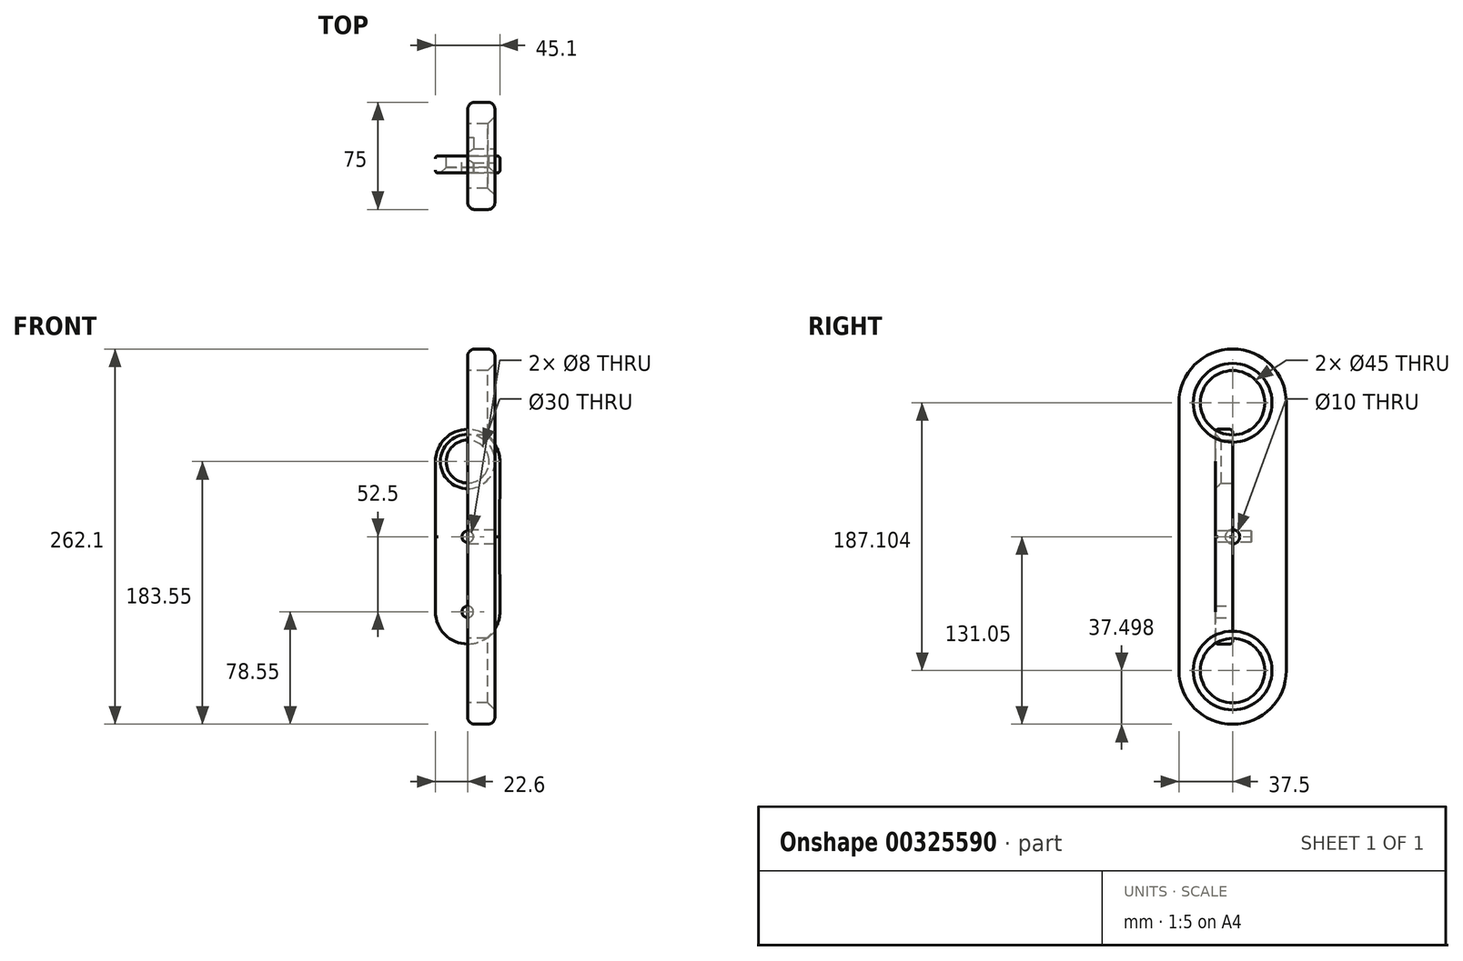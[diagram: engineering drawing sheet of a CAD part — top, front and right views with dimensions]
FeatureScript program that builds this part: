
annotation { "Feature Type Name" : "Feature", "Feature Type Description" : "" }
export const myFeature = defineFeature(function(context is Context, id is Id, definition is map)
    precondition{}
    {
        {
            var Q0;
            Q0=qCreatedBy(makeId("Right.planeOp"),FACE);
            var sketch = newSketch(context, id + "F0", { "sketchPlane" : qUnion([Q0])});
            skCircle(sketch, "E0", {"center": v(0, 93.55) * mm, "radius": 22.5 * mm});
            skArc(sketch, "E1", {"start": v(37.5, 93.55) * mm, "mid": v(0, 131.05) * mm, "end": v(-37.5, 93.55) * mm});
            skLineSegment(sketch, "E2", {"start": v(-37.5, 93.55) * mm, "end": v(-37.5, 0) * mm});
            skLineSegment(sketch, "E3", {"start": v(37.5, 0) * mm, "end": v(37.5, 93.55) * mm});
            skCircle(sketch, "E4.MirrorC", {"center": v(0, -93.55) * mm, "radius": 22.5 * mm});
            skArc(sketch, "E5.MirrorCS", {"start": v(37.5, -93.55) * mm, "mid": v(0, -131.05) * mm, "end": v(-37.5, -93.55) * mm});
            skLineSegment(sketch, "E6.MirrorCS", {"start": v(-37.5, -93.55) * mm, "end": v(-37.5, 0) * mm});
            skLineSegment(sketch, "E7.MirrorCS", {"start": v(37.5, 0) * mm, "end": v(37.5, -93.55) * mm});
            skSolve(sketch);
        }
        {
            var Q0;
            Q0 = qSketchRegion(id + "F0", true);
            extrude(context, id + "F1", {"entities" : qUnion([Q0]), "depth" : 19 * mm});
        }
        {
            var Q0;
            Q0=makeQuery(id+"F1.opExtrude","CAP_EDGE",EDGE,{"disambiguationData":[OSD([sQuery(id+"F0.wireOp",EDGE,"E0")])],"isStart":false});
            var Q1;
            Q1=makeQuery(id+"F1.opExtrude","CAP_EDGE",EDGE,{"disambiguationData":[OSD([sQuery(id+"F0.wireOp",EDGE,"E4.MirrorC")])],"isStart":false});
            chamfer(context, id + "F2", {"entities" : qUnion([Q0, Q1]), "width" : 5 * mm, "tangentPropagation" : true});
        }
        {
            var Q0;
            Q0=qCreatedBy(makeId("Right.planeOp"),FACE);
            var sketch = newSketch(context, id + "F3", { "sketchPlane" : qUnion([Q0])});
            skCircle(sketch, "E8", {"center": v(0, 0) * mm, "radius": 5 * mm});
            skSolve(sketch);
        }
        {
            var Q0;
            Q0 = qSketchRegion(id + "F3", true);
            extrude(context, id + "F4", {"entities" : qUnion([Q0]), "operationType" : NewBodyOperationType.REMOVE, "endBound" : BoundingType.SYMMETRIC, "oppositeDirection" : true, "depth" : 40 * mm});
        }
        {
            var Q0;
            Q0=makeQuery(id+"F1.opExtrude","CAP_EDGE",EDGE,{"disambiguationData":[OSD([sQuery(id+"F0.wireOp",EDGE,"E2"),sQuery(id+"F0.wireOp",EDGE,"E6.MirrorCS")])],"isStart":false});
            var Q1;
            Q1=makeQuery(id+"F1.opExtrude","CAP_EDGE",EDGE,{"disambiguationData":[OSD([sQuery(id+"F0.wireOp",EDGE,"E1")])],"isStart":true});
            fillet(context, id + "F5", {"entities" : qUnion([Q0, Q1]), "radius" : 5 * mm, "tangentPropagation" : true, "allowEdgeOverflow" : false});
        }
        {
            var Q0;
            Q0=qCreatedBy(makeId("Front.planeOp"),FACE);
            var sketch = newSketch(context, id + "F6", { "sketchPlane" : qUnion([Q0])});
            skCircle(sketch, "E9", {"center": v(0, 52.5) * mm, "radius": 15 * mm});
            skArc(sketch, "E10", {"start": v(22.5, 52.46) * mm, "mid": v(0.04, 75) * mm, "end": v(-22.5, 52.54) * mm});
            skLineSegment(sketch, "E11", {"start": v(-22.6, 0) * mm, "end": v(-22.5, 52.54) * mm});
            skLineSegment(sketch, "E12", {"start": v(22.4, 0) * mm, "end": v(22.5, 52.46) * mm});
            skLineSegment(sketch, "E13.MirrorCS", {"start": v(22.4, 0) * mm, "end": v(22.5, -52.46) * mm});
            skArc(sketch, "E14.MirrorC", {"start": v(22.5, -52.46) * mm, "mid": v(0.04, -75) * mm, "end": v(-22.5, -52.54) * mm});
            skLineSegment(sketch, "E15.MirrorCS", {"start": v(-22.6, 0) * mm, "end": v(-22.5, -52.54) * mm});
            skCircle(sketch, "E16", {"center": v(0, -52.5) * mm, "radius": 4 * mm});
            skSolve(sketch);
        }
        {
            var Q0;
            Q0 = qSketchRegion(id + "F6", true);
            extrude(context, id + "F7", {"entities" : qUnion([Q0]), "depth" : 12 * mm});
        }
        {
            var Q0;
            Q0=makeQuery(id+"F7.opExtrude","CAP_EDGE",EDGE,{"disambiguationData":[OSD([sQuery(id+"F6.wireOp",EDGE,"E9")])],"isStart":false});
            chamfer(context, id + "F8", {"entities" : qUnion([Q0]), "width" : 4 * mm, "tangentPropagation" : true});
        }
        {
            var Q0;
            Q0=makeQuery(id+"F7.opExtrude","CAP_EDGE",EDGE,{"disambiguationData":[OSD([sQuery(id+"F6.wireOp",EDGE,"E11")])],"isStart":false});
            var Q1;
            Q1=makeQuery(id+"F7.opExtrude","CAP_EDGE",EDGE,{"disambiguationData":[OSD([sQuery(id+"F6.wireOp",EDGE,"E12")])],"isStart":true});
            var Q2;
            Q2=makeQuery(id+"F7.opExtrude","CAP_EDGE",EDGE,{"disambiguationData":[OSD([sQuery(id+"F6.wireOp",EDGE,"E14.MirrorC")])],"isStart":false});
            var Q3;
            Q3=makeQuery(id+"F7.opExtrude","CAP_EDGE",EDGE,{"disambiguationData":[OSD([sQuery(id+"F6.wireOp",EDGE,"E14.MirrorC")])],"isStart":true});
            fillet(context, id + "F9", {"entities" : qUnion([Q0, Q1, Q2, Q3]), "radius" : 2 * mm, "tangentPropagation" : true, "allowEdgeOverflow" : false});
        }
        {
            var Q0;
            Q0=makeQuery(id+"F7.opExtrude","CAP_FACE",FACE,{"disambiguationData":[OSD([sQuery(id+"F6.wireOp",EDGE,"E9"),sQuery(id+"F6.wireOp",EDGE,"E10"),sQuery(id+"F6.wireOp",EDGE,"E11"),sQuery(id+"F6.wireOp",EDGE,"E12"),sQuery(id+"F6.wireOp",EDGE,"E13.MirrorCS"),sQuery(id+"F6.wireOp",EDGE,"E14.MirrorC"),sQuery(id+"F6.wireOp",EDGE,"E15.MirrorCS"),sQuery(id+"F6.wireOp",EDGE,"E16")])],"isStart":false});
            var sketch = newSketch(context, id + "F10", { "sketchPlane" : qUnion([Q0])});
            skCircle(sketch, "E17", {"center": v(0, 0) * mm, "radius": 4 * mm});
            skSolve(sketch);
        }
        {
            var Q0;
            Q0 = qSketchRegion(id + "F10", true);
            extrude(context, id + "F11", {"entities" : qUnion([Q0]), "operationType" : NewBodyOperationType.REMOVE, "oppositeDirection" : true, "depth" : 25 * mm});
        }
    });
